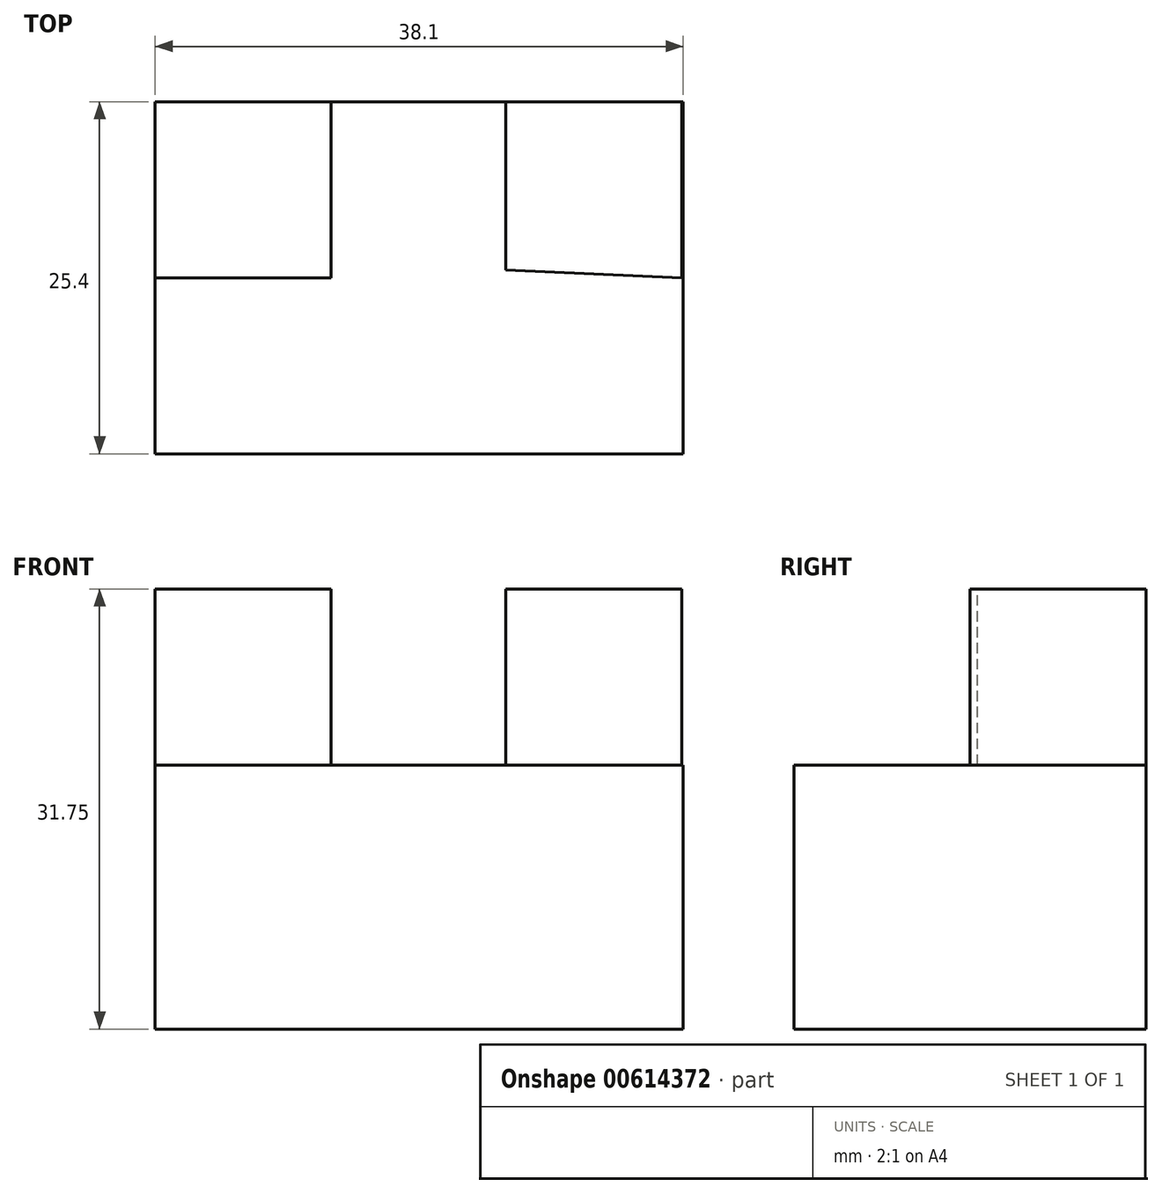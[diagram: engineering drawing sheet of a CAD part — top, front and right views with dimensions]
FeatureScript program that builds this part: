
annotation { "Feature Type Name" : "Feature", "Feature Type Description" : "" }
export const myFeature = defineFeature(function(context is Context, id is Id, definition is map)
    precondition{}
    {
        {
            var Q0;
            Q0=qCreatedBy(makeId("Front.planeOp"),FACE);
            var sketch = newSketch(context, id + "F0", { "sketchPlane" : qUnion([Q0])});
            skLineSegment(sketch, "E0", {"start": v(0, 0) * mm, "end": v(0, 31.75) * mm});
            skLineSegment(sketch, "E1", {"start": v(0, 0) * mm, "end": v(38.1, 0) * mm});
            skLineSegment(sketch, "E2", {"start": v(38.1, 0) * mm, "end": v(38.1, 31.75) * mm});
            skLineSegment(sketch, "E3", {"start": v(0, 31.75) * mm, "end": v(38.1, 31.75) * mm});
            skSolve(sketch);
        }
        {
            var Q0;
            Q0=makeQuery(id+"F0.imprint","IMPRINT",FACE,{"disambiguationData":[TD([[makeQuery(id+"F0.imprint","IMPRINT",EDGE,{"derivedFrom":sQuery(id+"F0.wireOp",EDGE,"E0")}),-1.0]])]});
            extrude(context, id + "F1", {"entities" : qUnion([Q0]), "depth" : 25.4 * mm, "offsetDistance" : 25.4 * mm});
        }
        {
            var Q0;
            Q0=makeQuery(id+"F1.opExtrude","SWEPT_FACE",FACE,{"disambiguationData":[OSD([sQuery(id+"F0.wireOp",EDGE,"E3")])]});
            var sketch = newSketch(context, id + "F2", { "sketchPlane" : qUnion([Q0])});
            skLineSegment(sketch, "E4", {"start": v(0, 0) * mm, "end": v(12.7, 0) * mm});
            skLineSegment(sketch, "E5", {"start": v(12.7, 0) * mm, "end": v(12.7, -12.7) * mm});
            skLineSegment(sketch, "E6", {"start": v(12.7, -12.7) * mm, "end": v(0, -12.7) * mm});
            skLineSegment(sketch, "E7", {"start": v(0, -12.7) * mm, "end": v(0, 0) * mm});
            skSolve(sketch);
        }
        {
            var Q0;
            {var subQ5=sQuery(id+"F2.wireOp",EDGE,"E5");Q0=makeQuery(id+"F2.imprint","IMPRINT",FACE,{"disambiguationData":[TD([[makeQuery(id+"F2.imprint","IMPRINT",EDGE,{"derivedFrom":subQ5}),1.0]])]});}
            var sketch = newSketch(context, id + "F3", { "sketchPlane" : qUnion([Q0])});
            skLineSegment(sketch, "E8", {"start": v(37.99, -12.7) * mm, "end": v(37.99, 0) * mm});
            skLineSegment(sketch, "E9", {"start": v(37.99, 0) * mm, "end": v(25.3, 0) * mm});
            skLineSegment(sketch, "E10", {"start": v(25.3, 0) * mm, "end": v(25.3, -12.16) * mm});
            skLineSegment(sketch, "E11", {"start": v(25.3, -12.16) * mm, "end": v(37.99, -12.7) * mm});
            skSolve(sketch);
        }
        {
            var Q0;
            {var subQ3=sQuery(id+"F3.wireOp",EDGE,"E8");Q0=makeQuery(id+"F3.imprint","IMPRINT",FACE,{"disambiguationData":[TD([[makeQuery(id+"F3.imprint","IMPRINT",EDGE,{"derivedFrom":subQ3}),-1.0]])]});}
            extrude(context, id + "F4", {"entities" : qUnion([Q0]), "operationType" : NewBodyOperationType.REMOVE, "oppositeDirection" : true, "depth" : 25.4 * mm, "offsetDistance" : 25.4 * mm});
        }
        {
            var Q0;
            Q0=makeQuery(id+"F4.boolean.opBoolean","COPY",FACE,{"derivedFrom":makeQuery(id+"F4.opExtrude","CAP_FACE",FACE,{"disambiguationData":[OSD([sQuery(id+"F0.wireOp",EDGE,"E0"),sQuery(id+"F0.wireOp",EDGE,"E2"),sQuery(id+"F0.wireOp",EDGE,"E3"),sQuery(id+"F2.wireOp",EDGE,"E5"),sQuery(id+"F2.wireOp",EDGE,"E6"),sQuery(id+"F3.wireOp",EDGE,"E8"),sQuery(id+"F3.wireOp",EDGE,"E10"),sQuery(id+"F3.wireOp",EDGE,"E11")])],"isStart":false})});
            extrude(context, id + "F5", {"entities" : qUnion([Q0]), "operationType" : NewBodyOperationType.ADD, "depth" : 12.7 * mm, "offsetDistance" : 25.4 * mm});
        }
    });
